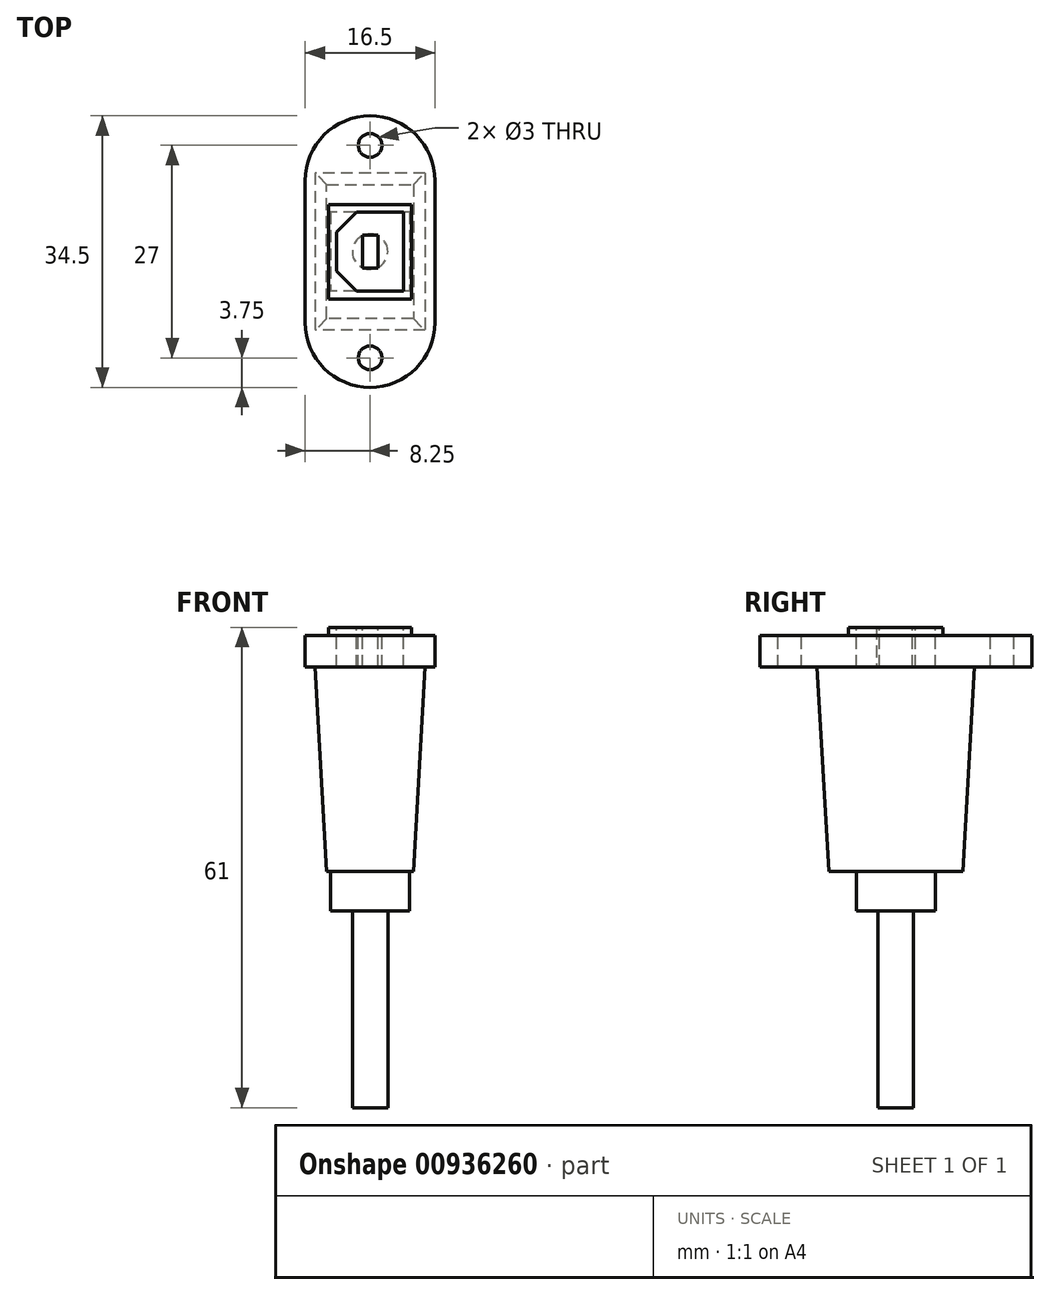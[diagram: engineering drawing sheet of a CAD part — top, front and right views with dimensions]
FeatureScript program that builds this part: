
annotation { "Feature Type Name" : "Feature", "Feature Type Description" : "" }
export const myFeature = defineFeature(function(context is Context, id is Id, definition is map)
    precondition{}
    {
        {
            var Q0;
            Q0=qCreatedBy(makeId("Top.planeOp"),FACE);
            var sketch = newSketch(context, id + "F0", { "sketchPlane" : qUnion([Q0])});
            skPoint(sketch, "E0.middle", {"position": v(0, 0) * mm});
            skLineSegment(sketch, "E1.bottom", {"start": v(8.25, -9) * mm, "end": v(-8.25, -9) * mm});
            skLineSegment(sketch, "E1.top", {"start": v(8.25, 9) * mm, "end": v(-8.25, 9) * mm});
            skArc(sketch, "E2", {"start": v(8.25, 9) * mm, "mid": v(0, 17.25) * mm, "end": v(-8.25, 9) * mm});
            skArc(sketch, "E3", {"start": v(8.25, -9) * mm, "mid": v(0, -17.25) * mm, "end": v(-8.25, -9) * mm});
            skCircle(sketch, "E4", {"center": v(0, 13.5) * mm, "radius": 1.5 * mm});
            skCircle(sketch, "E5", {"center": v(0, -13.5) * mm, "radius": 1.5 * mm});
            skSolve(sketch);
        }
        {
            var Q0;
            Q0=makeQuery(id+"F0.imprint","IMPRINT",FACE,{"disambiguationData":[TD([[makeQuery(id+"F0.imprint","IMPRINT",EDGE,{"derivedFrom":sQuery(id+"F0.wireOp",EDGE,"E0.bottom")}),1.0]])]});
            var Q1;
            Q1=makeQuery(id+"F0.imprint","IMPRINT",FACE,{"disambiguationData":[TD([[makeQuery(id+"F0.imprint","IMPRINT",EDGE,{"derivedFrom":sQuery(id+"F0.wireOp",EDGE,"E1.top")}),-1.0]])]});
            var Q2;
            Q2=makeQuery(id+"F0.imprint","IMPRINT",FACE,{"disambiguationData":[TD([[makeQuery(id+"F0.imprint","IMPRINT",EDGE,{"derivedFrom":sQuery(id+"F0.wireOp",EDGE,"E1.bottom")}),1.0]])]});
            extrude(context, id + "F1", {"entities" : qUnion([Q0, Q1, Q2]), "oppositeDirection" : true, "depth" : 4 * mm, "offsetDistance" : 25 * mm});
        }
        {
            var Q0;
            Q0=makeQuery(id+"F1.opExtrude","CAP_FACE",FACE,{"disambiguationData":[OSD([sQuery(id+"F0.wireOp",EDGE,"E0.bottom"),sQuery(id+"F0.wireOp",EDGE,"E0.top"),sQuery(id+"F0.wireOp",EDGE,"E0.left"),sQuery(id+"F0.wireOp",EDGE,"E0.right"),sQuery(id+"F0.wireOp",EDGE,"E1.left"),sQuery(id+"F0.wireOp",EDGE,"E1.right"),sQuery(id+"F0.wireOp",EDGE,"E2"),sQuery(id+"F0.wireOp",EDGE,"E3"),sQuery(id+"F0.wireOp",EDGE,"E4"),sQuery(id+"F0.wireOp",EDGE,"E5")])],"isStart":false});
            var sketch = newSketch(context, id + "F2", { "sketchPlane" : qUnion([Q0])});
            skLineSegment(sketch, "E6.bottom", {"start": v(7, -10) * mm, "end": v(-7, -10) * mm});
            skLineSegment(sketch, "E6.top", {"start": v(7, 10) * mm, "end": v(-7, 10) * mm});
            skLineSegment(sketch, "E6.left", {"start": v(7, -10) * mm, "end": v(7, 10) * mm});
            skLineSegment(sketch, "E6.right", {"start": v(-7, -10) * mm, "end": v(-7, 10) * mm});
            skPoint(sketch, "E6.middle", {"position": v(0, 0) * mm});
            skSolve(sketch);
        }
        {
            var Q0;
            Q0=qSketchRegion(id+"F2",true);
            extrude(context, id + "F3", {"entities" : qUnion([Q0]), "operationType" : NewBodyOperationType.ADD, "depth" : 26 * mm, "offsetDistance" : 25 * mm});
        }
        {
            var Q0;
            Q0=makeQuery(id+"F3.opExtrude","CAP_EDGE",EDGE,{"disambiguationData":[OSD([sQuery(id+"F2.wireOp",EDGE,"E6.top")])],"isStart":false});
            var Q1;
            Q1=makeQuery(id+"F3.opExtrude","CAP_EDGE",EDGE,{"disambiguationData":[OSD([sQuery(id+"F2.wireOp",EDGE,"E6.bottom")])],"isStart":false});
            var Q2;
            Q2=makeQuery(id+"F3.opExtrude","CAP_EDGE",EDGE,{"disambiguationData":[OSD([sQuery(id+"F2.wireOp",EDGE,"E6.left")])],"isStart":false});
            var Q3;
            Q3=makeQuery(id+"F3.opExtrude","CAP_EDGE",EDGE,{"disambiguationData":[OSD([sQuery(id+"F2.wireOp",EDGE,"E6.right")])],"isStart":false});
            chamfer(context, id + "F4", {"entities" : qUnion([Q0, Q1, Q2, Q3]), "chamferType" : ChamferType.TWO_OFFSETS, "width1" : 1.5 * mm, "oppositeDirection" : false, "width2" : 26 * mm, "tangentPropagation" : true});
        }
        {
            var Q0;
            Q0=makeQuery(id+"F3.opExtrude","CAP_FACE",FACE,{"disambiguationData":[OSD([sQuery(id+"F2.wireOp",EDGE,"E6.bottom"),sQuery(id+"F2.wireOp",EDGE,"E6.top"),sQuery(id+"F2.wireOp",EDGE,"E6.left"),sQuery(id+"F2.wireOp",EDGE,"E6.right")])],"isStart":false});
            var sketch = newSketch(context, id + "F5", { "sketchPlane" : qUnion([Q0])});
            skLineSegment(sketch, "E7.bottom", {"start": v(5, -5) * mm, "end": v(-5, -5) * mm});
            skLineSegment(sketch, "E7.top", {"start": v(5, 5) * mm, "end": v(-5, 5) * mm});
            skLineSegment(sketch, "E7.left", {"start": v(5, -5) * mm, "end": v(5, 5) * mm});
            skLineSegment(sketch, "E7.right", {"start": v(-5, -5) * mm, "end": v(-5, 5) * mm});
            skPoint(sketch, "E7.middle", {"position": v(0, 0) * mm});
            skSolve(sketch);
        }
        {
            var Q0;
            Q0=qSketchRegion(id+"F5",true);
            extrude(context, id + "F6", {"entities" : qUnion([Q0]), "operationType" : NewBodyOperationType.ADD, "depth" : 5 * mm, "offsetDistance" : 25 * mm});
        }
        {
            var Q0;
            Q0=makeQuery(id+"F6.opExtrude","CAP_FACE",FACE,{"disambiguationData":[OSD([sQuery(id+"F5.wireOp",EDGE,"E7.bottom"),sQuery(id+"F5.wireOp",EDGE,"E7.top"),sQuery(id+"F5.wireOp",EDGE,"E7.left"),sQuery(id+"F5.wireOp",EDGE,"E7.right")])],"isStart":false});
            var sketch = newSketch(context, id + "F7", { "sketchPlane" : qUnion([Q0])});
            skCircle(sketch, "E8", {"center": v(0, 0) * mm, "radius": 2.25 * mm});
            skSolve(sketch);
        }
        {
            var Q0;
            Q0=qSketchRegion(id+"F7",true);
            extrude(context, id + "F8", {"entities" : qUnion([Q0]), "operationType" : NewBodyOperationType.ADD, "depth" : 25 * mm, "offsetDistance" : 25 * mm});
        }
        {
            var Q0;
            Q0=makeQuery(id+"F1.opExtrude","SWEPT_FACE",FACE,{"disambiguationData":[OSD([sQuery(id+"F0.wireOp",EDGE,"E1.bottom")])]});
            extrude(context, id + "F9", {"entities" : qUnion([Q0]), "operationType" : NewBodyOperationType.ADD, "depth" : 18 * mm, "offsetDistance" : 25 * mm});
        }
        {
            var Q0;
            {var subQ0=sQuery(id+"F0.wireOp",EDGE,"E1.bottom");Q0=makeQuery(id+"F9.boolean.opBoolean","MERGE",FACE,{"derivedFrom":[makeQuery(id+"F1.opExtrude","CAP_FACE",FACE,{"disambiguationData":[OSD([subQ0,sQuery(id+"F0.wireOp",EDGE,"E3"),sQuery(id+"F0.wireOp",EDGE,"E5")])],"isStart":true}),makeQuery(id+"F1.opExtrude","CAP_FACE",FACE,{"disambiguationData":[OSD([sQuery(id+"F0.wireOp",EDGE,"E1.top"),sQuery(id+"F0.wireOp",EDGE,"E2"),sQuery(id+"F0.wireOp",EDGE,"E4")])],"isStart":true}),makeQuery(id+"F9.opExtrude","SWEPT_FACE",FACE,{"disambiguationData":[OSD([subQ0]),TDD([makeQuery(id+"F1.opExtrude","CAP_EDGE",EDGE,{"disambiguationData":[OSD([subQ0])],"isStart":true})])]})]});}
            var sketch = newSketch(context, id + "F10", { "sketchPlane" : qUnion([Q0])});
            skLineSegment(sketch, "E9.bottom", {"start": v(5.25, 6) * mm, "end": v(-5.25, 6) * mm});
            skLineSegment(sketch, "E9.top", {"start": v(5.25, -6) * mm, "end": v(-5.25, -6) * mm});
            skLineSegment(sketch, "E9.left", {"start": v(5.25, 6) * mm, "end": v(5.25, -6) * mm});
            skLineSegment(sketch, "E9.right", {"start": v(-5.25, 6) * mm, "end": v(-5.25, -6) * mm});
            skPoint(sketch, "E9.middle", {"position": v(0, 0) * mm});
            skSolve(sketch);
        }
        {
            var Q0;
            Q0=qSketchRegion(id+"F10",true);
            extrude(context, id + "F11", {"entities" : qUnion([Q0]), "operationType" : NewBodyOperationType.ADD, "depth" : 1 * mm, "offsetDistance" : 25 * mm});
        }
        {
            var Q0;
            Q0=makeQuery(id+"F11.opExtrude","CAP_FACE",FACE,{"disambiguationData":[OSD([sQuery(id+"F10.wireOp",EDGE,"E9.bottom"),sQuery(id+"F10.wireOp",EDGE,"E9.top"),sQuery(id+"F10.wireOp",EDGE,"E9.left"),sQuery(id+"F10.wireOp",EDGE,"E9.right")])],"isStart":false});
            var sketch = newSketch(context, id + "F12", { "sketchPlane" : qUnion([Q0])});
            skSolve(sketch);
        }
        {
            var Q0;
            Q0=makeQuery(id+"F12.imprint","IMPRINT",FACE,{"disambiguationData":[TD([[makeQuery(id+"F12.imprint","IMPRINT",EDGE,{"derivedFrom":makeQuery(id+"F11.opExtrude","CAP_EDGE",EDGE,{"disambiguationData":[OSD([sQuery(id+"F10.wireOp",EDGE,"E9.bottom")])],"isStart":false})}),1.0]])]});
            var sketch = newSketch(context, id + "F13", { "sketchPlane" : qUnion([Q0])});
            skLineSegment(sketch, "E10.bottom", {"start": v(4.25, -5) * mm, "end": v(-4.25, -5) * mm});
            skLineSegment(sketch, "E10.top", {"start": v(4.25, 5) * mm, "end": v(-4.25, 5) * mm});
            skLineSegment(sketch, "E10.left", {"start": v(4.25, -5) * mm, "end": v(4.25, 5) * mm});
            skLineSegment(sketch, "E10.right", {"start": v(-4.25, -5) * mm, "end": v(-4.25, 5) * mm});
            skPoint(sketch, "E10.middle", {"position": v(0, 0) * mm});
            skLineSegment(sketch, "E11.bottom", {"start": v(0.99, -2.11) * mm, "end": v(-0.99, -2.11) * mm});
            skLineSegment(sketch, "E11.top", {"start": v(0.99, 2.11) * mm, "end": v(-0.99, 2.11) * mm});
            skLineSegment(sketch, "E11.left", {"start": v(0.99, -2.11) * mm, "end": v(0.99, 2.11) * mm});
            skLineSegment(sketch, "E11.right", {"start": v(-0.99, -2.11) * mm, "end": v(-0.99, 2.11) * mm});
            skSolve(sketch);
        }
        {
            var Q0;
            Q0=qSketchRegion(id+"F13",true);
            extrude(context, id + "F14", {"entities" : qUnion([Q0]), "operationType" : NewBodyOperationType.REMOVE, "oppositeDirection" : true, "depth" : 5 * mm, "offsetDistance" : 25 * mm});
        }
        {
            var Q0;
            Q0=makeQuery(id+"F14.boolean.opBoolean","COPY",EDGE,{"derivedFrom":makeQuery(id+"F14.opExtrude","SWEPT_EDGE",EDGE,{"disambiguationData":[OSD([sQuery(id+"F13.wireOp",EDGE,"E10.bottom"),sQuery(id+"F13.wireOp",EDGE,"E10.right")])]})});
            var Q1;
            Q1=makeQuery(id+"F14.boolean.opBoolean","COPY",EDGE,{"derivedFrom":makeQuery(id+"F14.opExtrude","SWEPT_EDGE",EDGE,{"disambiguationData":[OSD([sQuery(id+"F13.wireOp",EDGE,"E10.top"),sQuery(id+"F13.wireOp",EDGE,"E10.right")])]})});
            chamfer(context, id + "F15", {"entities" : qUnion([Q0, Q1]), "width" : 2.5 * mm, "tangentPropagation" : true});
        }
    });
